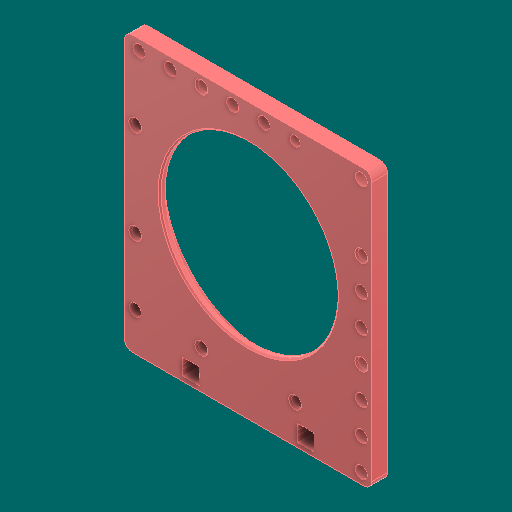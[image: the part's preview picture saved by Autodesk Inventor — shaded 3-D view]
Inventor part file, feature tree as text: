
AUTODESK INVENTOR PART (.ipt)
format: ipt  version: 2023.1 (Build 271208000, 208)  size: 247,808 bytes
history: native  units: in
note: dims shown in document units (in); Inventor stores cm internally (conversion verified against a paired STEP export)
features: other x3, sketch x2
ambient origin geometry x8: Origin, YZ Plane, XZ Plane, XY Plane, X Axis, Y Axis, Z Axis, Center Point
bodies: Solid1 (feature_tree)
feature tree (5):
  other  "Baseplate.ipt"
  other  "Solid1::Baseplate.ipt"
  other  "TaggingFeature1"
  sketch  "Sketch1"  dims[d0=0.3937in]
  sketch  "Sketch2"
